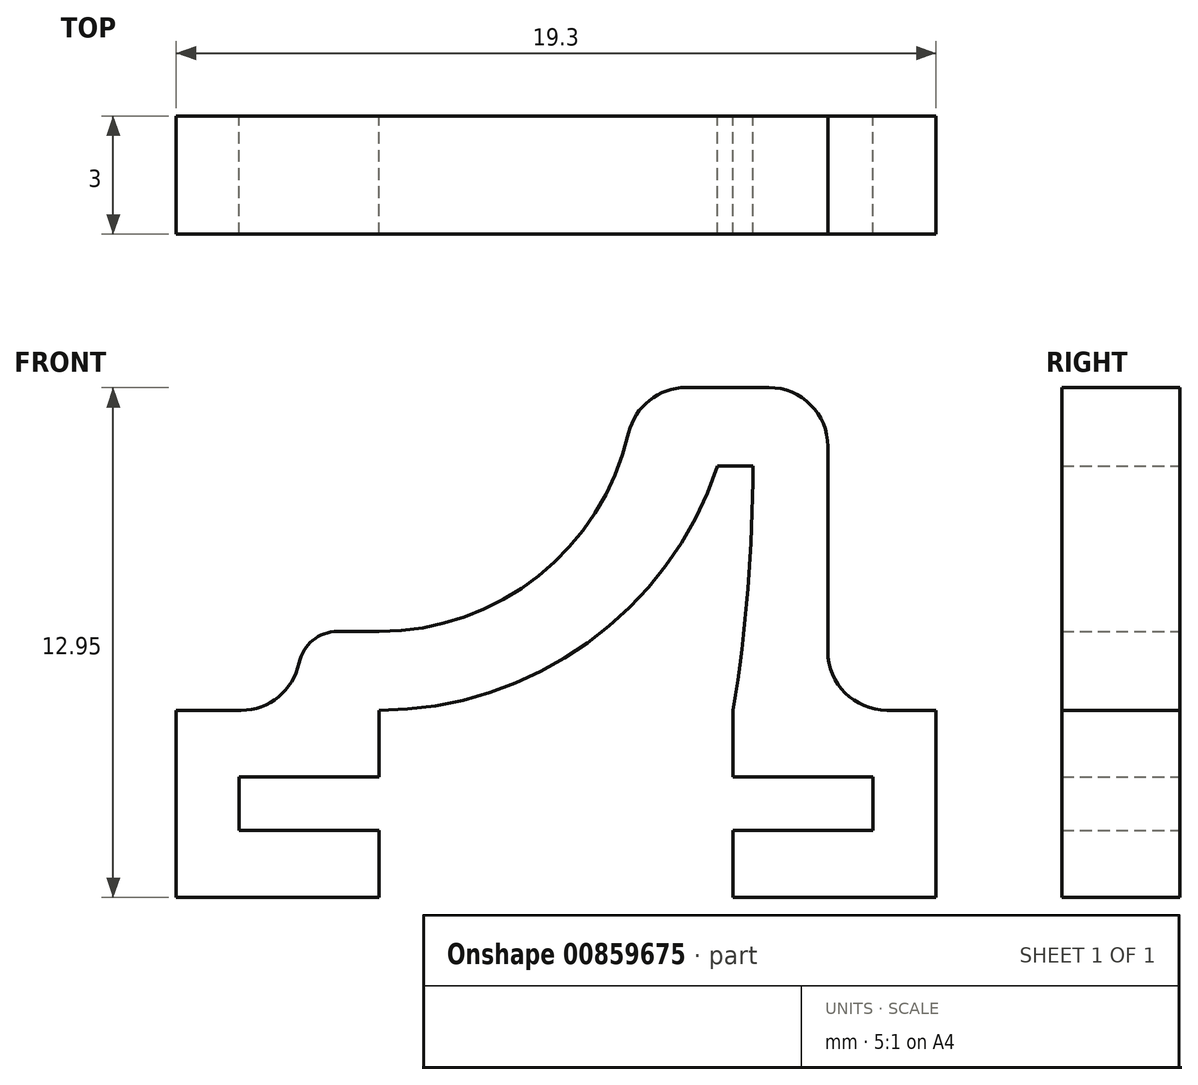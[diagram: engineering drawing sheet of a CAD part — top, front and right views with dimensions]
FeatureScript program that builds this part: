
annotation { "Feature Type Name" : "Feature", "Feature Type Description" : "" }
export const myFeature = defineFeature(function(context is Context, id is Id, definition is map)
    precondition{}
    {
        {
            var Q0;
            Q0=qCreatedBy(makeId("Front.planeOp"),FACE);
            var sketch = newSketch(context, id + "F0", { "sketchPlane" : qUnion([Q0])});
            skLineSegment(sketch, "E0.bottom", {"start": v(8.05, -0.67) * mm, "end": v(4.5, -0.67) * mm});
            skLineSegment(sketch, "E0.top", {"start": v(8.05, 0.68) * mm, "end": v(4.5, 0.68) * mm});
            skLineSegment(sketch, "E0.left", {"start": v(8.05, -0.67) * mm, "end": v(8.05, 0.68) * mm});
            skLineSegment(sketch, "E0.right", {"start": v(-8.05, -0.68) * mm, "end": v(-8.05, 0.67) * mm});
            skPoint(sketch, "E0.middle", {"position": v(0, 0) * mm});
            skLineSegment(sketch, "E1.bottom", {"start": v(9.65, -2.37) * mm, "end": v(4.5, -2.37) * mm});
            skLineSegment(sketch, "E1.top", {"start": v(9.65, 2.38) * mm, "end": v(6.9, 2.38) * mm});
            skLineSegment(sketch, "E1.left", {"start": v(9.65, -2.37) * mm, "end": v(9.65, 2.38) * mm});
            skLineSegment(sketch, "E1.right", {"start": v(-9.65, -2.38) * mm, "end": v(-9.65, 2.37) * mm});
            skLineSegment(sketch, "E2.left", {"start": v(4.5, -2.37) * mm, "end": v(4.5, -0.67) * mm});
            skLineSegment(sketch, "E2.right", {"start": v(-4.5, -2.38) * mm, "end": v(-4.5, -0.68) * mm});
            skLineSegment(sketch, "E3.top", {"start": v(4.9, 10.58) * mm, "end": v(6.9, 10.58) * mm});
            skLineSegment(sketch, "E3.right", {"start": v(6.9, 2.38) * mm, "end": v(6.9, 10.58) * mm});
            skLineSegment(sketch, "E4.top", {"start": v(-4.5, 4.37) * mm, "end": v(-6.5, 4.37) * mm});
            skLineSegment(sketch, "E4.right", {"start": v(-6.5, 2.37) * mm, "end": v(-6.5, 4.37) * mm});
            skLineSegment(sketch, "E5", {"start": v(4.1, 8.58) * mm, "end": v(5, 8.58) * mm});
            skLineSegment(sketch, "E6", {"start": v(2, 10.58) * mm, "end": v(4.9, 10.58) * mm});
            skArc(sketch, "E7", {"start": v(-4.5, 2.37) * mm, "mid": v(0.8, 4.09) * mm, "end": v(4.1, 8.58) * mm});
            skArc(sketch, "E8", {"start": v(-4.5, 4.37) * mm, "mid": v(0, 6.17) * mm, "end": v(2, 10.58) * mm});
            skArc(sketch, "E9", {"start": v(4.5, 2.38) * mm, "mid": v(4.87, 5.46) * mm, "end": v(5, 8.58) * mm});
            skLineSegment(sketch, "E10.trimOffspring", {"start": v(-4.5, -2.38) * mm, "end": v(-9.65, -2.38) * mm});
            skLineSegment(sketch, "E11.trimOffspring", {"start": v(-4.5, -0.68) * mm, "end": v(-8.05, -0.68) * mm});
            skLineSegment(sketch, "E12.trimOffspring", {"start": v(-4.5, 0.68) * mm, "end": v(-4.5, 2.37) * mm});
            skLineSegment(sketch, "E13.trimOffspring", {"start": v(4.5, 0.68) * mm, "end": v(4.5, 2.38) * mm});
            skLineSegment(sketch, "E14.trimOffspring", {"start": v(-4.5, 0.68) * mm, "end": v(-8.05, 0.67) * mm});
            skLineSegment(sketch, "E15.trimOffspring", {"start": v(-6.5, 2.37) * mm, "end": v(-9.65, 2.37) * mm});
            skPoint(sketch, "E16.trimOffspring.start.orphan", {"position": v(5, 2.28) * mm});
            skSolve(sketch);
        }
        {
            var Q0;
            Q0=makeQuery(id+"F0.imprint","IMPRINT",FACE,{"disambiguationData":[TD([[makeQuery(id+"F0.imprint","IMPRINT",EDGE,{"derivedFrom":sQuery(id+"F0.wireOp",EDGE,"E0.bottom")}),1.0]])]});
            extrude(context, id + "F1", {"entities" : qUnion([Q0]), "depth" : 3 * mm, "offsetDistance" : 25 * mm});
        }
        {
            var Q0;
            Q0=makeQuery(id+"F1.opExtrude","SWEPT_EDGE",EDGE,{"disambiguationData":[OSD([sQuery(id+"F0.wireOp",EDGE,"E4.right"),sQuery(id+"F0.wireOp",EDGE,"E15.trimOffspring")])]});
            var Q1;
            Q1=makeQuery(id+"F1.opExtrude","SWEPT_EDGE",EDGE,{"disambiguationData":[OSD([sQuery(id+"F0.wireOp",EDGE,"E1.top"),sQuery(id+"F0.wireOp",EDGE,"E3.right")])]});
            var Q2;
            Q2=makeQuery(id+"F1.opExtrude","SWEPT_EDGE",EDGE,{"disambiguationData":[OSD([sQuery(id+"F0.wireOp",EDGE,"E3.top"),sQuery(id+"F0.wireOp",EDGE,"E3.right")])]});
            var Q3;
            Q3=makeQuery(id+"F1.opExtrude","SWEPT_EDGE",EDGE,{"disambiguationData":[OSD([sQuery(id+"F0.wireOp",EDGE,"E6"),sQuery(id+"F0.wireOp",EDGE,"E8")])]});
            fillet(context, id + "F2", {"entities" : qUnion([Q0, Q1, Q2, Q3]), "radius" : 1.5 * mm, "tangentPropagation" : true, "allowEdgeOverflow" : false});
        }
        {
            var Q0;
            Q0=makeQuery(id+"F1.opExtrude","SWEPT_EDGE",EDGE,{"disambiguationData":[OSD([sQuery(id+"F0.wireOp",EDGE,"E4.top"),sQuery(id+"F0.wireOp",EDGE,"E4.right")])]});
            fillet(context, id + "F3", {"entities" : qUnion([Q0]), "radius" : 1 * mm, "tangentPropagation" : true, "allowEdgeOverflow" : false});
        }
    });
